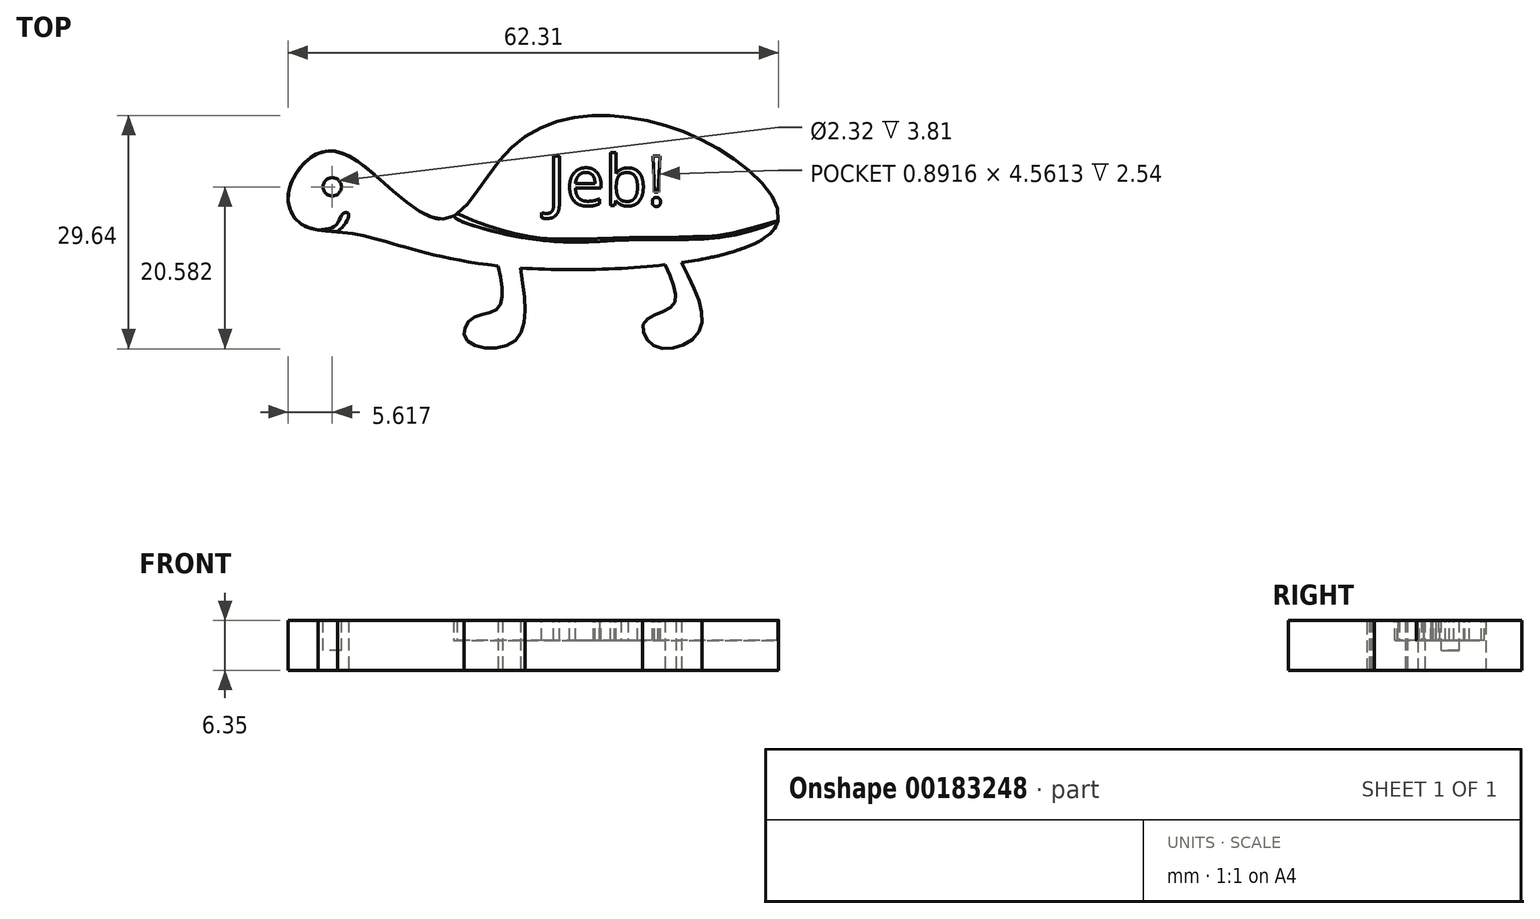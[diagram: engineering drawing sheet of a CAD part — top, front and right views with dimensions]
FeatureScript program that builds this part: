
annotation { "Feature Type Name" : "Feature", "Feature Type Description" : "" }
export const myFeature = defineFeature(function(context is Context, id is Id, definition is map)
    precondition{}
    {
        {
            var Q0;
            Q0=qCreatedBy(makeId("Top.planeOp"),FACE);
            var sketch = newSketch(context, id + "F0", { "sketchPlane" : qUnion([Q0])});
            skFitSpline(sketch, "E0", {"points": [v(-37.27, -5.14) * mm, v(-43.57, -3.98) * mm, v(-45.22, 0) * mm, v(-41.91, 4.8) * mm, v(-36.6, 4.14) * mm, v(-25.51, -3.31) * mm, v(-17.23, 5.47) * mm, v(-3.64, 9.77) * mm, v(12.1, 3.81) * mm, v(16.57, -4.47) * mm, v(-18.55, -9.28) * mm, v(-37.27, -5.14) * mm]});
            skFitSpline(sketch, "E1", {"points": [v(-18.55, -9.28) * mm, v(-18.55, -14.58) * mm, v(-22.03, -16.07) * mm, v(-22.53, -18.72) * mm, v(-16.57, -18.88) * mm, v(-15.74, -9.52) * mm], "startDerivative": vector(6.67, -32.34) * mm, "endDerivative": vector(-6.82, 43.84) * mm});
            skFitSpline(sketch, "E2", {"points": [v(2.65, -9.11) * mm, v(3.64, -14.25) * mm, v(0, -16.4) * mm, v(1.5, -19.55) * mm, v(6.96, -17.56) * mm, v(4.7, -8.85) * mm], "startDerivative": vector(14.21, -31.26) * mm, "endDerivative": vector(-19.97, 38.3) * mm});
            skSolve(sketch);
        }
        {
            var Q0;
            Q0 = qSketchRegion(id + "F0", true);
            extrude(context, id + "F1", {"entities" : qUnion([Q0]), "depth" : 6.35 * mm});
        }
        {
            var Q0;
            Q0=makeQuery(id+"F1.opExtrude","CAP_FACE",FACE,{"disambiguationData":[OSD([sQuery(id+"F0.wireOp",EDGE,"E0"),sQuery(id+"F0.wireOp",EDGE,"E1"),sQuery(id+"F0.wireOp",EDGE,"E2")])],"isStart":false});
            var sketch = newSketch(context, id + "F2", { "sketchPlane" : qUnion([Q0])});
            skCircle(sketch, "E3", {"center": v(-39.64, 0.78) * mm, "radius": 1.16 * mm});
            skSolve(sketch);
        }
        {
            var Q0;
            Q0 = qSketchRegion(id + "F2", true);
            extrude(context, id + "F3", {"entities" : qUnion([Q0]), "operationType" : NewBodyOperationType.REMOVE, "oppositeDirection" : true, "depth" : 3.8 * mm});
        }
        {
            var Q0;
            Q0=makeQuery(id+"F1.opExtrude","CAP_FACE",FACE,{"disambiguationData":[OSD([sQuery(id+"F0.wireOp",EDGE,"E0"),sQuery(id+"F0.wireOp",EDGE,"E1"),sQuery(id+"F0.wireOp",EDGE,"E2")])],"isStart":false});
            var sketch = newSketch(context, id + "F4", { "sketchPlane" : qUnion([Q0])});
            skFitSpline(sketch, "E4", {"points": [v(-41.45, -4.68) * mm, v(-39.15, -4.07) * mm, v(-38.28, -2.6) * mm, v(-37.64, -2.56) * mm, v(-37.7, -3.4) * mm, v(-38.97, -4.93) * mm], "startDerivative": vector(10.5, 0.61) * mm, "endDerivative": vector(-6.52, -6.46) * mm});
            skFitSpline(sketch, "E5", {"points": [v(-41.45, -4.68) * mm, v(-38.97, -4.93) * mm], "startDerivative": vector(2.48, -0.25) * mm, "endDerivative": vector(2.48, -0.25) * mm});
            skSolve(sketch);
        }
        {
            var Q0;
            Q0 = qSketchRegion(id + "F4", true);
            extrude(context, id + "F5", {"entities" : qUnion([Q0]), "operationType" : NewBodyOperationType.REMOVE, "oppositeDirection" : true, "depth" : 6.35 * mm});
        }
        {
            var Q0;
            {var subQ0=sQuery(id+"F0.wireOp",EDGE,"E2");var subQ1=sQuery(id+"F0.wireOp",EDGE,"E1");var subQ2=sQuery(id+"F0.wireOp",EDGE,"E0");Q0=makeQuery(id+"F5.boolean.opBoolean","SPLIT",FACE,{"disambiguationData":[TD([makeQuery(id+"F1.opExtrude","SWEPT_FACE",FACE,{"disambiguationData":[OSD([subQ1])]})])],"derivedFrom":makeQuery(id+"F1.opExtrude","CAP_FACE",FACE,{"disambiguationData":[OSD([subQ2,subQ1,subQ0])],"isStart":false})});}
            var sketch = newSketch(context, id + "F6", { "sketchPlane" : qUnion([Q0])});
            skFitSpline(sketch, "E6", {"points": [v(-24.23, -2.92) * mm, v(-13.65, -5.95) * mm, v(-1.12, -5.92) * mm, v(11.33, -5.37) * mm, v(16.98, -3.53) * mm, v(11.4, -5.06) * mm, v(7.15, -5.52) * mm, v(2.05, -5.68) * mm, v(-4.58, -5.71) * mm, v(-9.69, -5.87) * mm, v(-14.42, -5.55) * mm, v(-18.29, -4.66) * mm, v(-22.83, -3.03) * mm, v(-23.78, -2.64) * mm, v(-24.23, -2.92) * mm]});
            skSolve(sketch);
        }
        {
            var Q0;
            Q0 = qSketchRegion(id + "F6", true);
            extrude(context, id + "F7", {"entities" : qUnion([Q0]), "operationType" : NewBodyOperationType.REMOVE, "oppositeDirection" : true, "depth" : 2.54 * mm});
        }
        {
            var Q0;
            {var subQ0=sQuery(id+"F0.wireOp",EDGE,"E1");var subQ1=sQuery(id+"F0.wireOp",EDGE,"E0");var subQ2=sQuery(id+"F0.wireOp",EDGE,"E2");var subQ3=makeQuery(id+"F1.opExtrude","SWEPT_FACE",FACE,{"disambiguationData":[OSD([subQ1]),TDD([makeQuery(id+"F0.imprint","IMPRINT",EDGE,{"disambiguationData":[TD([[makeQuery(id+"F0.imprint","INTERSECT",VERTEX,{"disambiguationData":[OD(0.0)],"derivedFrom":[subQ1,subQ0]}),-1.0]])],"derivedFrom":subQ1})])]});Q0=makeQuery(id+"F7.boolean.opBoolean","SPLIT",FACE,{"disambiguationData":[TD([subQ3,makeQuery(id+"F7.opExtrude","SWEPT_FACE",FACE,{"disambiguationData":[OSD([sQuery(id+"F6.wireOp",EDGE,"E6")])]})])],"derivedFrom":makeQuery(id+"F5.boolean.opBoolean","SPLIT",FACE,{"disambiguationData":[TD([makeQuery(id+"F1.opExtrude","SWEPT_FACE",FACE,{"disambiguationData":[OSD([subQ0])]})])],"derivedFrom":makeQuery(id+"F1.opExtrude","CAP_FACE",FACE,{"disambiguationData":[OSD([subQ1,subQ0,subQ2])],"isStart":false})})});}
            var sketch = newSketch(context, id + "F8", { "sketchPlane" : qUnion([Q0])});
            skText(sketch, "E7", { "text": "Jeb!", "fontName": "OpenSans-Regular.ttf"});
            const initialGuessF8  = {"E7": [-0.01235, -0.0016, 1, 0, 0.00635]};
            skSetInitialGuess(sketch, initialGuessF8);
            skSolve(sketch);
        }
        {
            var Q0;
            Q0 = qSketchRegion(id + "F8", true);
            extrude(context, id + "F9", {"entities" : qUnion([Q0]), "operationType" : NewBodyOperationType.REMOVE, "oppositeDirection" : true, "depth" : 2.54 * mm});
        }
    });
